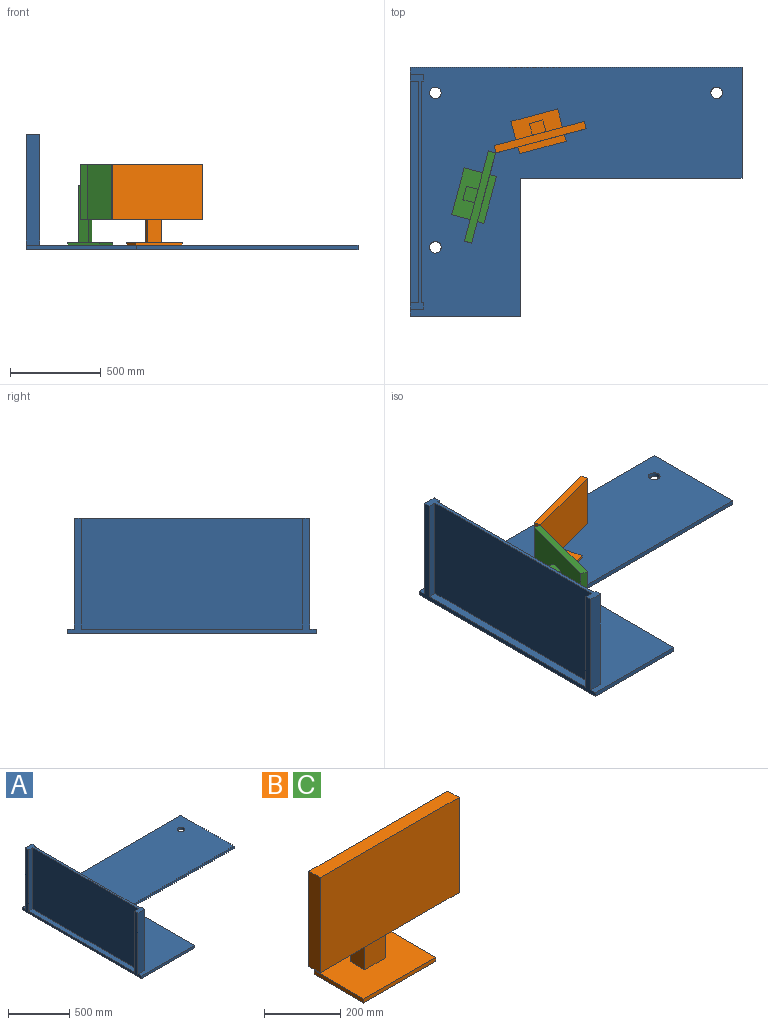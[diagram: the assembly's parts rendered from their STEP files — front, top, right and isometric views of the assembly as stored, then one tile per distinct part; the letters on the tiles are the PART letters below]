
ASSEMBLY  parts=3 mates=2
PART A: 23 faces, bbox 1828.8x1371.6x635 mm
  f0: plane 1828.8x1371.6mm, normal (0,0,1), area 1486625.3mm2, adj f2,f3,f4,f5,f6,f7,f8,f9
  f1: plane 1219.2x44.45mm, normal (0,0,1), area 54193.4mm2, adj f3,f12,f13,f14
  f2: plane 1828.8x25.4mm, normal (0,1,0), area 46451.5mm2, adj f0,f3,f9,f11
  f3: plane 1371.6x635mm, normal (-1,0,0), area 81290.2mm2, adj f0,f1,f2,f4,f11,f12,f14,f15
  f4: plane 609.6x25.4mm, normal (0,-1,0), area 15483.8mm2, adj f0,f3,f5,f11
  f5: plane 762x25.4mm, normal (1,0,0), area 19354.8mm2, adj f0,f4,f6,f11
  f6: plane 1219.2x25.4mm, normal (0,-1,0), area 30967.7mm2, adj f0,f5,f9,f11
  f7: cylinder r=31.75mm len=63.5mm, axis (0,0,1), area 5067.1mm2, adj f0,f11
  f8: cylinder r=31.75mm len=63.5mm, axis (0,0,1), area 5067.1mm2, adj f0,f11
  f9: plane 609.6x25.4mm, normal (1,0,0), area 15483.8mm2, adj f0,f2,f6,f11
  f10: cylinder r=31.75mm len=63.5mm, axis (0,0,1), area 5067.1mm2, adj f0,f11
  f11: plane 1828.8x1371.6mm, normal (0,0,-1), area 1569850.9mm2, adj f2,f3,f4,f5,f6,f7,f8,f9
  f12: plane 609.6x44.45mm, normal (0,-1,0), area 27096.7mm2, adj f1,f3,f13,f22
  f13: plane 1219.2x609.6mm, normal (-1,0,0), area 743224.3mm2, adj f1,f12,f14,f22
  f14: plane 609.6x44.45mm, normal (0,1,0), area 27096.7mm2, adj f1,f3,f13,f22
  f15: plane 609.6x76.2mm, normal (0,-1,0), area 46451.5mm2, adj f0,f3,f16,f22
  f16: plane 609.6x38.1mm, normal (1,0,0), area 23225.8mm2, adj f0,f15,f17,f22
  f17: plane 609.6x12.7mm, normal (0,1,0), area 7741.9mm2, adj f0,f16,f18,f22
  f18: plane 1219.2x609.6mm, normal (1,0,0), area 743224.3mm2, adj f0,f17,f19,f22
  f19: plane 609.6x12.7mm, normal (0,-1,0), area 7741.9mm2, adj f0,f18,f20,f22
  f20: plane 609.6x38.1mm, normal (1,0,0), area 23225.8mm2, adj f0,f19,f21,f22
  f21: plane 609.6x76.2mm, normal (0,1,0), area 46451.5mm2, adj f0,f3,f20,f22
  f22: plane 1295.4x76.2mm, normal (0,0,1), area 29032.2mm2, adj f3,f12,f13,f14,f15,f16,f17,f18
PART B: 18 faces, bbox 514.4x184.2x444.5 mm
  f0: plane 266.7x12.7mm, normal (0,-1,0), area 3387.1mm2, adj f1,f3,f4,f5
  f1: plane 184.15x12.7mm, normal (1,0,0), area 2338.7mm2, adj f0,f2,f4,f5
  f2: plane 266.7x12.7mm, normal (0,1,0), area 3387.1mm2, adj f1,f3,f4,f5
  f3: plane 184.15x12.7mm, normal (-1,0,0), area 2338.7mm2, adj f0,f2,f4,f5
  f4: plane 266.7x184.15mm, normal (0,0,1), area 44999.9mm2, adj f0,f1,f2,f3,f12,f13,f16,f17
  f5: plane 266.7x184.15mm, normal (0,0,-1), area 49112.8mm2, adj f0,f1,f2,f3
  f6: plane 514.35x304.8mm, normal (0,1,0), area 150967.4mm2, adj f7,f8,f9,f10,f14,f15,f16,f17
  f7: plane 514.35x41.28mm, normal (0,0,-1), area 21229.8mm2, adj f6,f8,f10,f11
  f8: plane 304.8x41.28mm, normal (1,0,0), area 12580.6mm2, adj f6,f7,f9,f11
  f9: plane 514.35x41.28mm, normal (0,0,1), area 21229.8mm2, adj f6,f8,f10,f11
  f10: plane 304.8x41.28mm, normal (-1,0,0), area 12580.6mm2, adj f6,f7,f9,f11
  f11: plane 514.35x304.8mm, normal (0,-1,0), area 156773.9mm2, adj f7,f8,f9,f10
  f12: plane 241.3x76.2mm, normal (0,-1,0), area 18387.1mm2, adj f4,f15,f16,f17
  f13: plane 317.5x76.2mm, normal (0,1,0), area 24193.5mm2, adj f4,f14,f16,f17
  f14: plane 76.2x66.68mm, normal (0,0,1), area 5080.6mm2, adj f6,f13,f16,f17
  f15: plane 76.2x12.7mm, normal (0,0,-1), area 967.7mm2, adj f6,f12,f16,f17
  f16: plane 317.5x66.68mm, normal (1,0,0), area 18104.8mm2, adj f4,f6,f12,f13,f14,f15
  f17: plane 317.5x66.68mm, normal (-1,0,0), area 18104.8mm2, adj f4,f6,f12,f13,f14,f15
PART C: same geometry as B
PLACE A at identity fixed
PLACE B rot(axis=(0,0,1),15deg) t=(708.38,-351.77,0)mm
PLACE C rot(axis=(0,0,1),75deg) t=(353.16,-705.58,0)mm
MATE planar C.f5 <-> A.f0  axis (0,0,-1) through (353.16,-705.58,0)mm
MATE planar B.f5 <-> A.f0  axis (0,0,-1) through (708.38,-351.77,0)mm
